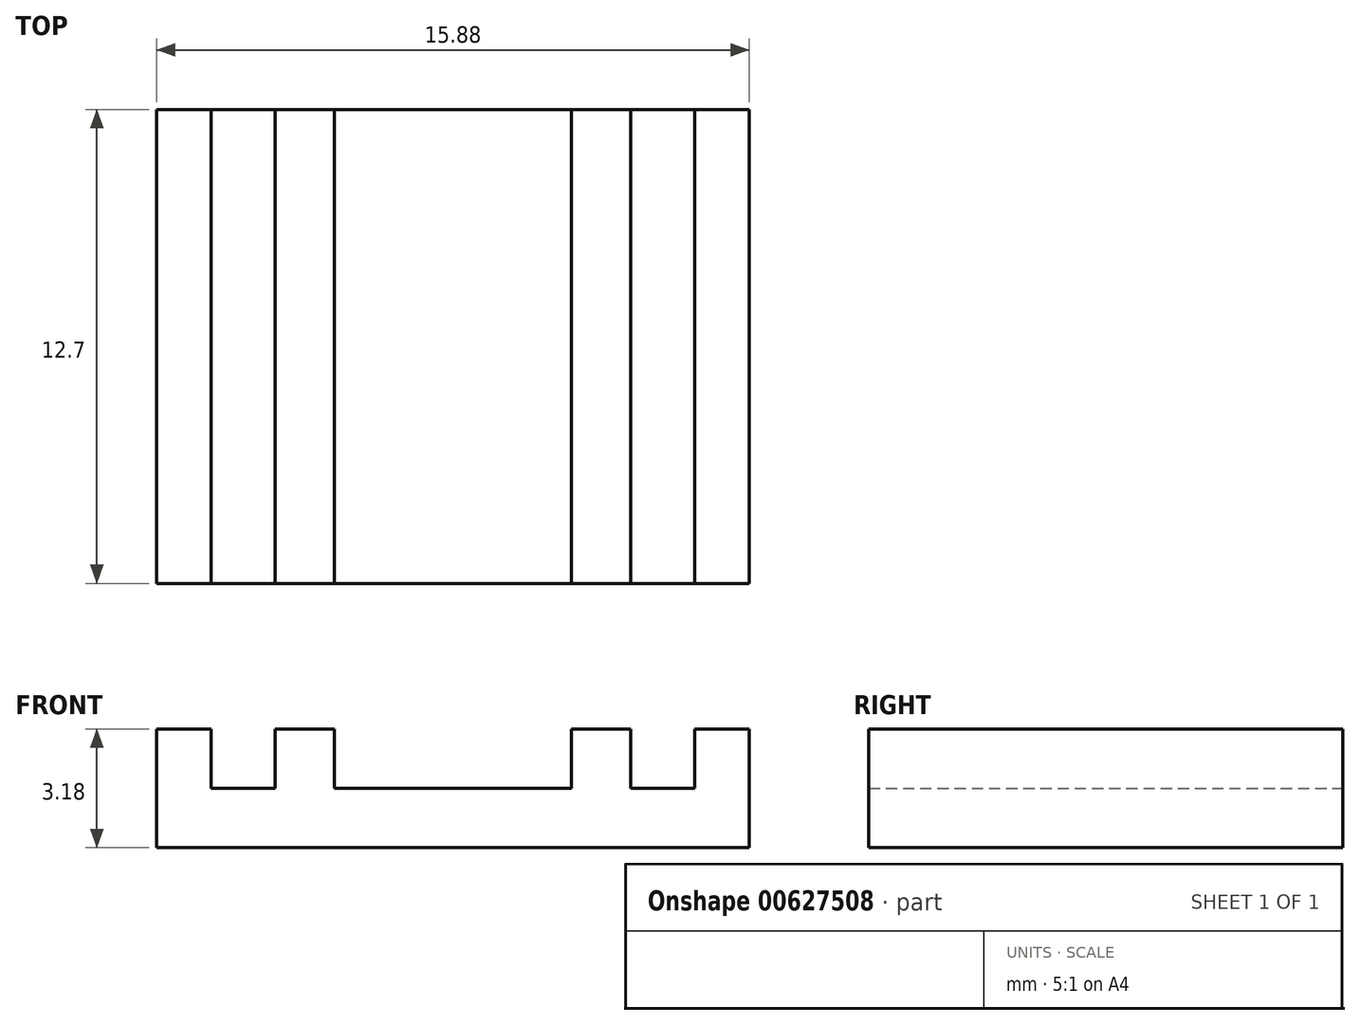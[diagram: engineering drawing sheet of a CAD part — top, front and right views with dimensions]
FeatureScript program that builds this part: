
annotation { "Feature Type Name" : "Feature", "Feature Type Description" : "" }
export const myFeature = defineFeature(function(context is Context, id is Id, definition is map)
    precondition{}
    {
        {
            var Q0;
            Q0=qCreatedBy(makeId("Front.planeOp"),FACE);
            var sketch = newSketch(context, id + "F0", { "sketchPlane" : qUnion([Q0])});
            skLineSegment(sketch, "E0.bottom", {"start": v(-7.94, -1.59) * mm, "end": v(7.94, -1.59) * mm});
            skLineSegment(sketch, "E0.top", {"start": v(-7.94, 1.59) * mm, "end": v(-6.48, 1.59) * mm});
            skLineSegment(sketch, "E0.left", {"start": v(-7.94, -1.59) * mm, "end": v(-7.94, 1.59) * mm});
            skLineSegment(sketch, "E0.right", {"start": v(7.94, -1.59) * mm, "end": v(7.94, 1.59) * mm});
            skPoint(sketch, "E0.middle", {"position": v(0, 0) * mm});
            skLineSegment(sketch, "E1.bottom", {"start": v(-6.48, 0) * mm, "end": v(-4.76, 0) * mm});
            skLineSegment(sketch, "E1.left", {"start": v(-6.48, 0) * mm, "end": v(-6.48, 1.59) * mm});
            skLineSegment(sketch, "E1.right", {"start": v(6.48, 0) * mm, "end": v(6.48, 1.59) * mm});
            skPoint(sketch, "E1.middle", {"position": v(0, 0.8) * mm});
            skLineSegment(sketch, "E2.top", {"start": v(4.76, 1.59) * mm, "end": v(3.18, 1.59) * mm});
            skLineSegment(sketch, "E2.left", {"start": v(4.76, 0) * mm, "end": v(4.76, 1.59) * mm});
            skLineSegment(sketch, "E2.right", {"start": v(3.18, 0) * mm, "end": v(3.18, 1.59) * mm});
            skLineSegment(sketch, "E3.MirrorCS", {"start": v(-3.18, 0) * mm, "end": v(-3.18, 1.59) * mm});
            skLineSegment(sketch, "E4.MirrorCS", {"start": v(-4.76, 0) * mm, "end": v(-4.76, 1.59) * mm});
            skLineSegment(sketch, "E5.trimOffspring", {"start": v(6.48, 1.59) * mm, "end": v(7.94, 1.59) * mm});
            skLineSegment(sketch, "E6.trimOffspring", {"start": v(3.18, 1.59) * mm, "end": v(4.76, 1.59) * mm});
            skLineSegment(sketch, "E7.trimOffspring", {"start": v(-4.76, 1.59) * mm, "end": v(-3.18, 1.59) * mm});
            skLineSegment(sketch, "E8.trimOffspring", {"start": v(4.76, 0) * mm, "end": v(6.48, 0) * mm});
            skLineSegment(sketch, "E9.trimOffspring", {"start": v(-3.18, 0) * mm, "end": v(3.18, 0) * mm});
            skSolve(sketch);
        }
        {
            var Q0;
            Q0 = qSketchRegion(id + "F0", true);
            extrude(context, id + "F1", {"entities" : qUnion([Q0]), "depth" : 12.7 * mm, "offsetDistance" : 25.4 * mm});
        }
    });
